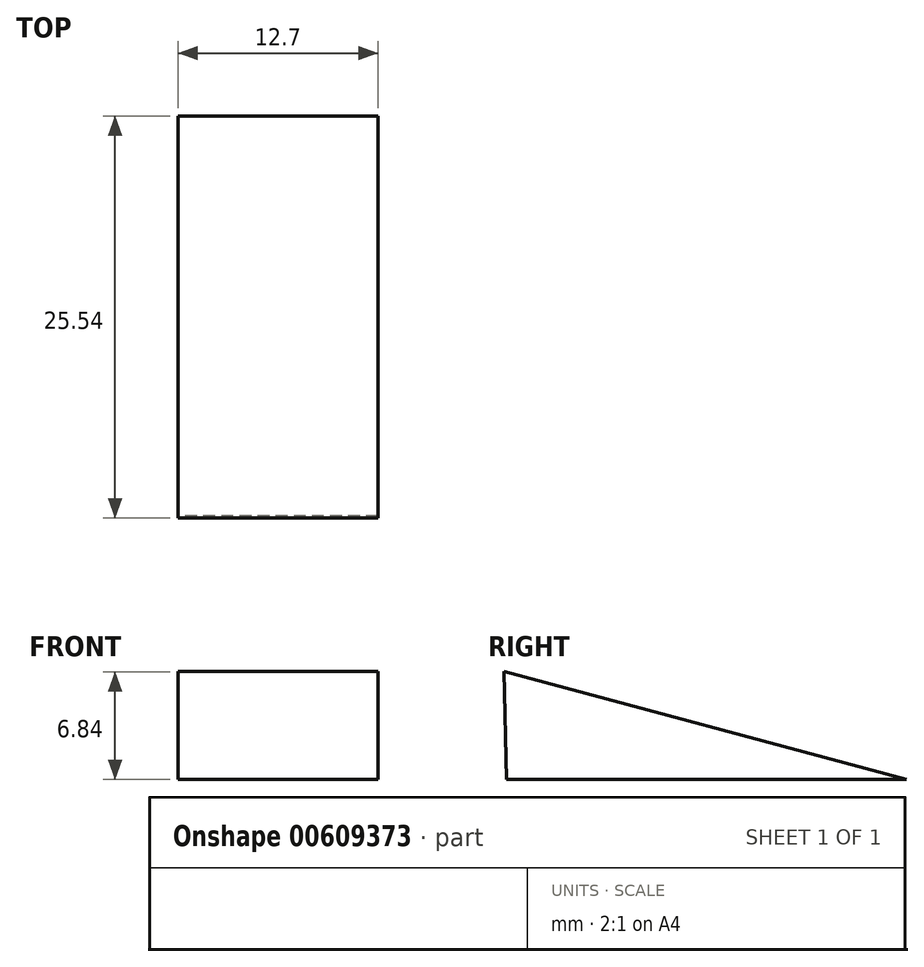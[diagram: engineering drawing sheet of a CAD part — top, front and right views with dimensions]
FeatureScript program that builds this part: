
annotation { "Feature Type Name" : "Feature", "Feature Type Description" : "" }
export const myFeature = defineFeature(function(context is Context, id is Id, definition is map)
    precondition{}
    {
        {
            var Q0;
            Q0=qCreatedBy(makeId("Right.planeOp"),FACE);
            var sketch = newSketch(context, id + "F0", { "sketchPlane" : qUnion([Q0])});
            skLineSegment(sketch, "E0", {"start": v(-12.69, 0) * mm, "end": v(12.71, 0) * mm});
            skLineSegment(sketch, "E1", {"start": v(12.71, 0) * mm, "end": v(-12.83, 6.84) * mm});
            skLineSegment(sketch, "E2", {"start": v(-12.83, 6.84) * mm, "end": v(-12.69, 0) * mm});
            skSolve(sketch);
        }
        {
            var Q0;
            Q0 = qSketchRegion(id + "F0", true);
            extrude(context, id + "F1", {"entities" : qUnion([Q0]), "depth" : 12.7 * mm, "offsetDistance" : 25.4 * mm});
        }
    });
